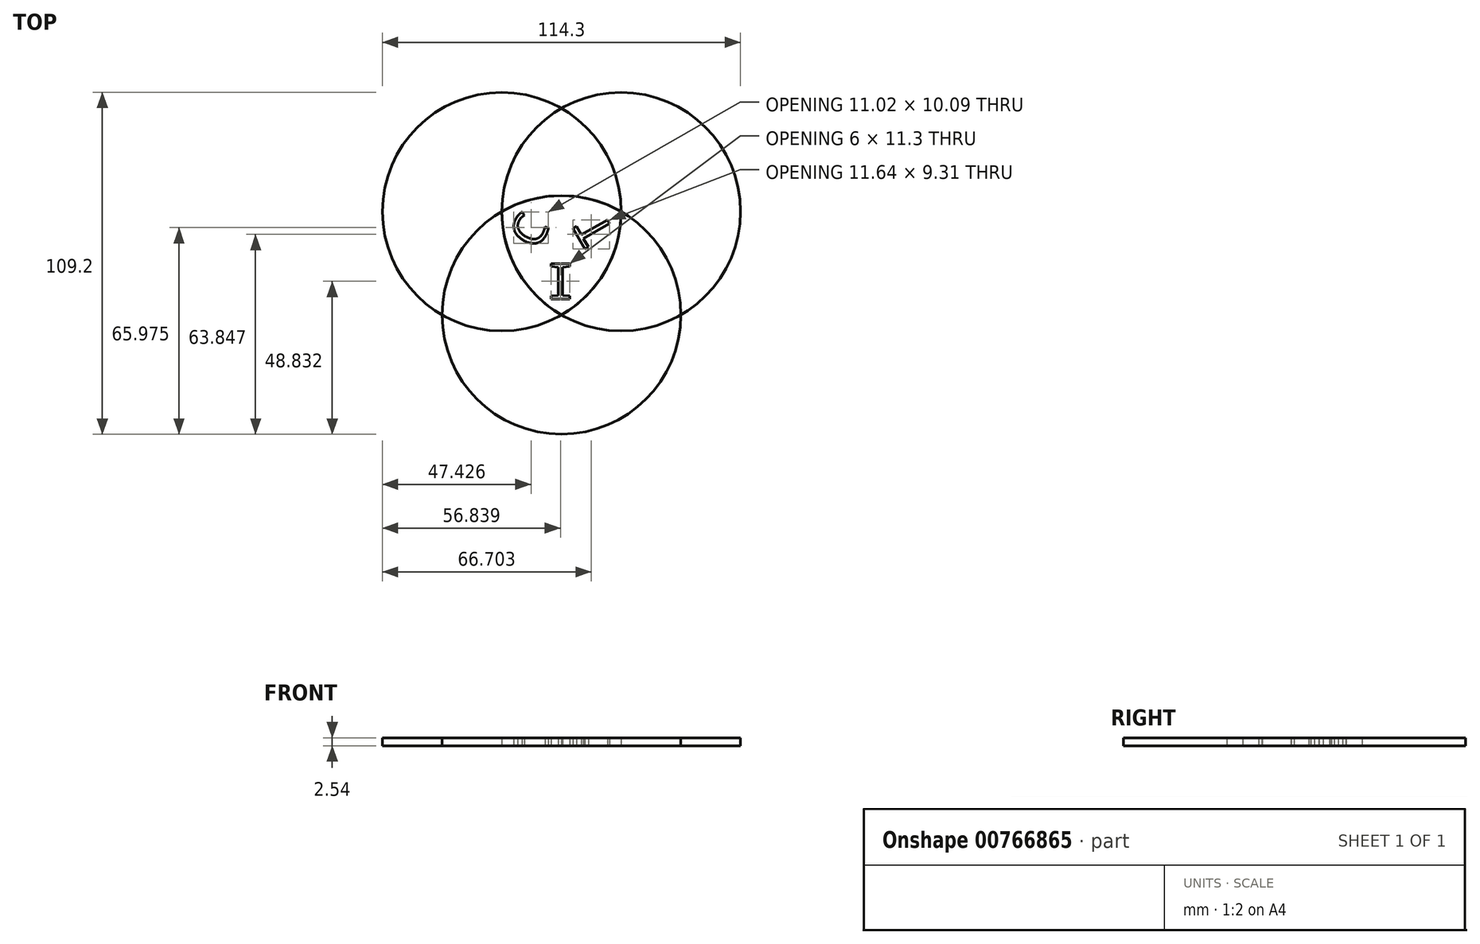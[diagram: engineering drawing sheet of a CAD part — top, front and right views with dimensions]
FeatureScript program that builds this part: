
annotation { "Feature Type Name" : "Feature", "Feature Type Description" : "" }
export const myFeature = defineFeature(function(context is Context, id is Id, definition is map)
    precondition{}
    {
        {
            var Q0;
            Q0=qCreatedBy(makeId("Top.planeOp"),FACE);
            var sketch = newSketch(context, id + "F0", { "sketchPlane" : qUnion([Q0])});
            skCircle(sketch, "E0", {"center": v(0, 0) * mm, "radius": 38.1 * mm});
            skSolve(sketch);
        }
        {
            var Q0;
            Q0=qCreatedBy(makeId("Top.planeOp"),FACE);
            var sketch = newSketch(context, id + "F1", { "sketchPlane" : qUnion([Q0])});
            skCircle(sketch, "E1", {"center": v(-38.1, 0) * mm, "radius": 38.1 * mm});
            skSolve(sketch);
        }
        {
            var Q0;
            Q0=qCreatedBy(makeId("Top.planeOp"),FACE);
            var sketch = newSketch(context, id + "F2", { "sketchPlane" : qUnion([Q0])});
            skCircle(sketch, "E2", {"center": v(-19.05, -33) * mm, "radius": 38.1 * mm});
            skSolve(sketch);
        }
        {
            var Q0;
            Q0 = qSketchRegion(id + "F0", true);
            extrude(context, id + "F3", {"entities" : qUnion([Q0]), "depth" : 2.54 * mm, "offsetDistance" : 25.4 * mm});
        }
        {
            var Q0;
            Q0=makeQuery(id+"F1.imprint","IMPRINT",FACE,{"disambiguationData":[TD([[makeQuery(id+"F1.imprint","IMPRINT",EDGE,{"derivedFrom":sQuery(id+"F1.wireOp",EDGE,"E1")}),1.0]])]});
            var Q1;
            Q1=sQuery(id+"F1.wireOp",EDGE,"E1");
            extrude(context, id + "F4", {"entities" : qUnion([Q0]), "surfaceEntities" : qUnion([Q1]), "depth" : 2.54 * mm, "offsetDistance" : 25.4 * mm});
        }
        {
            var Q0;
            Q0 = qSketchRegion(id + "F2", true);
            extrude(context, id + "F5", {"entities" : qUnion([Q0]), "depth" : 2.54 * mm, "offsetDistance" : 25.4 * mm});
        }
        {
            var Q0;
            Q0=makeQuery(id+"F3.opExtrude","SWEPT_BODY",BODY,{"disambiguationData":[OSD([sQuery(id+"F0.wireOp",EDGE,"E0")])]});
            var Q1;
            Q1=makeQuery(id+"F4.opExtrude","SWEPT_BODY",BODY,{"disambiguationData":[OSD([sQuery(id+"F1.wireOp",EDGE,"E1")])]});
            var Q2;
            Q2=makeQuery(id+"F5.opExtrude","SWEPT_BODY",BODY,{"disambiguationData":[OSD([sQuery(id+"F2.wireOp",EDGE,"E2")])]});
            booleanBodies(context, id + "F6", {"operationType" : BooleanOperationType.INTERSECTION, "tools" : qUnion([Q0, Q1, Q2]), "keepTools" : true});
        }
        {
            var Q0;
            Q0=qCreatedBy(makeId("Top.planeOp"),FACE);
            var sketch = newSketch(context, id + "F7", { "sketchPlane" : qUnion([Q0])});
            skText(sketch, "E3", { "text": "C", "fontName": "DroidSansMono.ttf"});
            skText(sketch, "E4", { "text": "I", "fontName": "DroidSansMono.ttf"});
            skText(sketch, "E5", { "text": "T", "fontName": "DroidSansMono.ttf"});
            const initialGuessF7  = {"E3": [-0.02711, -0.0126, 0.5, 0.86603, 0.01073], "E4": [-0.0241, -0.02792, 1, 0, 0.0114], "E5": [-0.00175, -0.00714, -0.5, 0.86603, 0.01094]};
            skSetInitialGuess(sketch, initialGuessF7);
            skSolve(sketch);
        }
        {
            var Q0;
            Q0 = qSketchRegion(id + "F7", true);
            extrude(context, id + "F8", {"entities" : qUnion([Q0]), "depth" : 2.54 * mm, "offsetDistance" : 25.4 * mm});
        }
        {
            var Q0;
            Q0=makeQuery(id+"F8.opExtrude","SWEPT_BODY",BODY,{"disambiguationData":[OSD([sQuery(id+"F7.wireOp",EDGE,"E3.sketch_text.stroke-0"),sQuery(id+"F7.wireOp",EDGE,"E3.sketch_text.stroke-1"),sQuery(id+"F7.wireOp",EDGE,"E3.sketch_text.stroke-2"),sQuery(id+"F7.wireOp",EDGE,"E3.sketch_text.stroke-3"),sQuery(id+"F7.wireOp",EDGE,"E3.sketch_text.stroke-4"),sQuery(id+"F7.wireOp",EDGE,"E3.sketch_text.stroke-5"),sQuery(id+"F7.wireOp",EDGE,"E3.sketch_text.stroke-6"),sQuery(id+"F7.wireOp",EDGE,"E3.sketch_text.stroke-7"),sQuery(id+"F7.wireOp",EDGE,"E3.sketch_text.stroke-8"),sQuery(id+"F7.wireOp",EDGE,"E3.sketch_text.stroke-9"),sQuery(id+"F7.wireOp",EDGE,"E3.sketch_text.stroke-10"),sQuery(id+"F7.wireOp",EDGE,"E3.sketch_text.stroke-11"),sQuery(id+"F7.wireOp",EDGE,"E3.sketch_text.stroke-12"),sQuery(id+"F7.wireOp",EDGE,"E3.sketch_text.stroke-13")])]});
            var Q1;
            Q1=makeQuery(id+"F8.opExtrude","SWEPT_BODY",BODY,{"disambiguationData":[OSD([sQuery(id+"F7.wireOp",EDGE,"E4.sketch_text.stroke-0"),sQuery(id+"F7.wireOp",EDGE,"E4.sketch_text.stroke-1"),sQuery(id+"F7.wireOp",EDGE,"E4.sketch_text.stroke-2"),sQuery(id+"F7.wireOp",EDGE,"E4.sketch_text.stroke-3"),sQuery(id+"F7.wireOp",EDGE,"E4.sketch_text.stroke-4"),sQuery(id+"F7.wireOp",EDGE,"E4.sketch_text.stroke-5"),sQuery(id+"F7.wireOp",EDGE,"E4.sketch_text.stroke-6"),sQuery(id+"F7.wireOp",EDGE,"E4.sketch_text.stroke-7"),sQuery(id+"F7.wireOp",EDGE,"E4.sketch_text.stroke-8"),sQuery(id+"F7.wireOp",EDGE,"E4.sketch_text.stroke-9"),sQuery(id+"F7.wireOp",EDGE,"E4.sketch_text.stroke-10"),sQuery(id+"F7.wireOp",EDGE,"E4.sketch_text.stroke-11")])]});
            var Q2;
            Q2=makeQuery(id+"F8.opExtrude","SWEPT_BODY",BODY,{"disambiguationData":[OSD([sQuery(id+"F7.wireOp",EDGE,"E5.sketch_text.stroke-0"),sQuery(id+"F7.wireOp",EDGE,"E5.sketch_text.stroke-1"),sQuery(id+"F7.wireOp",EDGE,"E5.sketch_text.stroke-2"),sQuery(id+"F7.wireOp",EDGE,"E5.sketch_text.stroke-3"),sQuery(id+"F7.wireOp",EDGE,"E5.sketch_text.stroke-4"),sQuery(id+"F7.wireOp",EDGE,"E5.sketch_text.stroke-5"),sQuery(id+"F7.wireOp",EDGE,"E5.sketch_text.stroke-6"),sQuery(id+"F7.wireOp",EDGE,"E5.sketch_text.stroke-7")])]});
            var Q3;
            Q3=makeQuery(id+"F6.opBoolean","INTERSECT",BODY,{"derivedFrom":[makeQuery(id+"F3.opExtrude","SWEPT_BODY",BODY,{"disambiguationData":[OSD([sQuery(id+"F0.wireOp",EDGE,"E0")])]}),makeQuery(id+"F4.opExtrude","SWEPT_BODY",BODY,{"disambiguationData":[OSD([sQuery(id+"F1.wireOp",EDGE,"E1")])]}),makeQuery(id+"F5.opExtrude","SWEPT_BODY",BODY,{"disambiguationData":[OSD([sQuery(id+"F2.wireOp",EDGE,"E2")])]})]});
            booleanBodies(context, id + "F9", {"operationType" : BooleanOperationType.SUBTRACTION, "tools" : qUnion([Q0, Q1, Q2]), "targets" : qUnion([Q3])});
        }
    });
